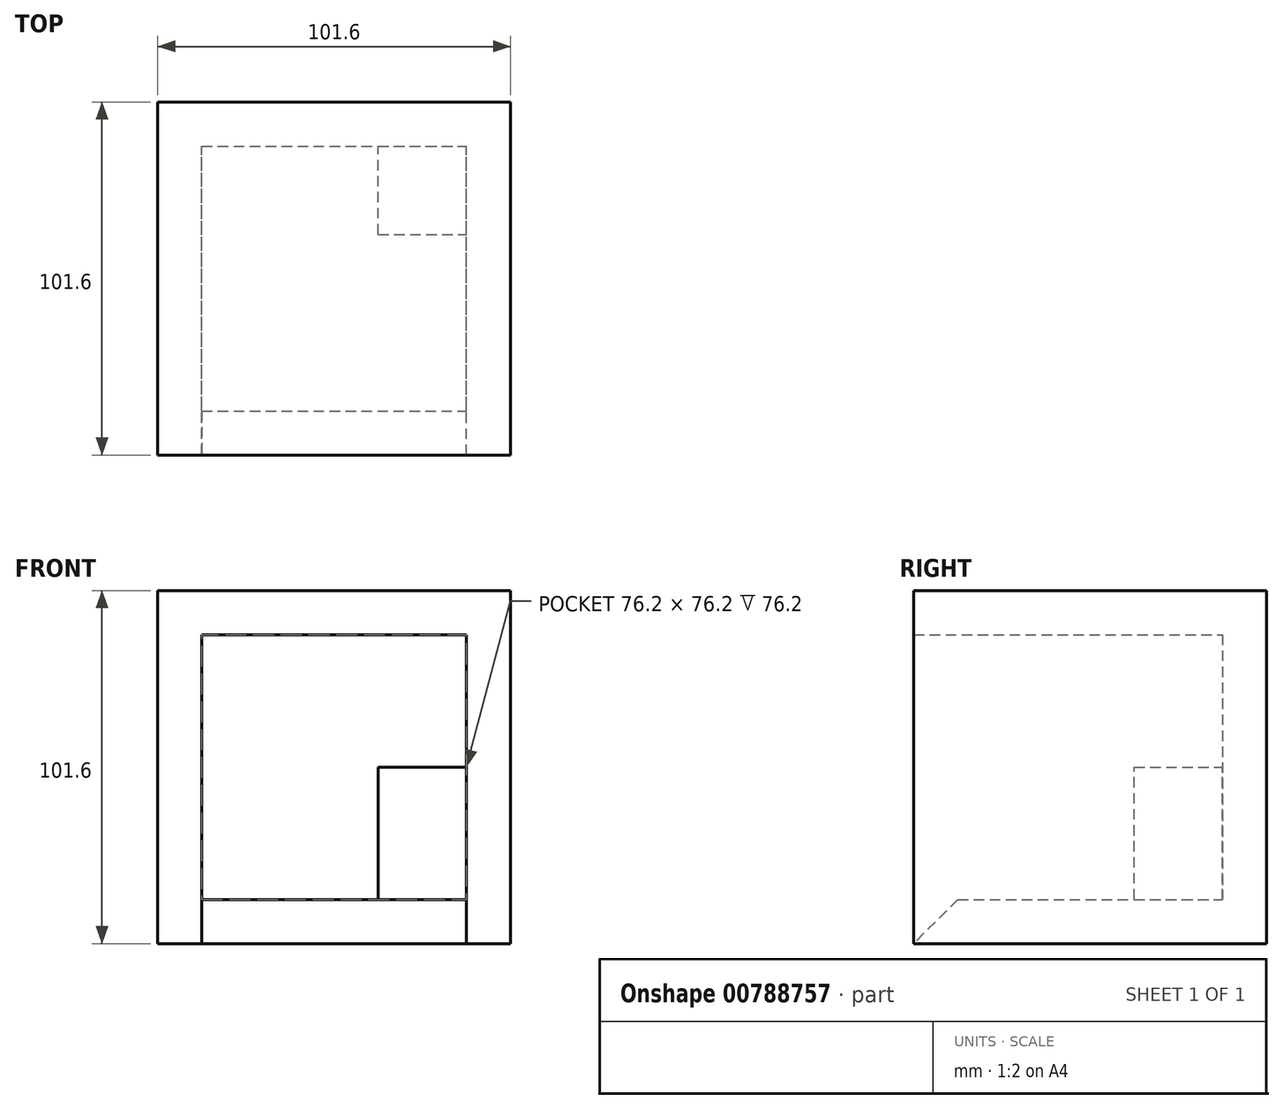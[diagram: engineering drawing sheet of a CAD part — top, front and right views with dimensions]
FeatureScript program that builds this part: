
annotation { "Feature Type Name" : "Feature", "Feature Type Description" : "" }
export const myFeature = defineFeature(function(context is Context, id is Id, definition is map)
    precondition{}
    {
        {
            var Q0;
            Q0=qCreatedBy(makeId("Front.planeOp"),FACE);
            var sketch = newSketch(context, id + "F0", { "sketchPlane" : qUnion([Q0])});
            skLineSegment(sketch, "E0.bottom", {"start": v(-44.9, 56.02) * mm, "end": v(56.7, 56.02) * mm});
            skLineSegment(sketch, "E0.top", {"start": v(-44.9, -45.58) * mm, "end": v(56.7, -45.58) * mm});
            skLineSegment(sketch, "E0.left", {"start": v(-44.9, 56.02) * mm, "end": v(-44.9, -45.58) * mm});
            skLineSegment(sketch, "E0.right", {"start": v(56.7, 56.02) * mm, "end": v(56.7, -45.58) * mm});
            skSolve(sketch);
        }
        {
            var Q0;
            Q0=makeQuery(id+"F0.imprint","IMPRINT",FACE,{"disambiguationData":[TD([[makeQuery(id+"F0.imprint","IMPRINT",EDGE,{"derivedFrom":sQuery(id+"F0.wireOp",EDGE,"E0.bottom")}),-1.0]])]});
            extrude(context, id + "F1", {"entities" : qUnion([Q0]), "depth" : 50.8 * mm, "offsetDistance" : 25.4 * mm, "hasSecondDirection" : true, "secondDirectionOppositeDirection" : true, "secondDirectionDepth" : 50.8 * mm});
        }
        {
            var Q0;
            Q0=makeQuery(id+"F1.opExtrude","CAP_FACE",FACE,{"disambiguationData":[OSD([sQuery(id+"F0.wireOp",EDGE,"E0.bottom"),sQuery(id+"F0.wireOp",EDGE,"E0.top"),sQuery(id+"F0.wireOp",EDGE,"E0.left"),sQuery(id+"F0.wireOp",EDGE,"E0.right")])],"isStart":false});
            shell(context, id + "F2", {"entities" : qUnion([Q0]), "thickness" : 12.7 * mm});
        }
        {
            var Q0;
            {var subQ0=sQuery(id+"F0.wireOp",EDGE,"E0.top");Q0=makeQuery(id+"F2.opShell","OFFSET_EDGE",EDGE,{"disambiguationData":[OSD([subQ0]),TDD([makeQuery(id+"F1.opExtrude","CAP_EDGE",EDGE,{"disambiguationData":[OSD([subQ0])],"isStart":false})])]});}
            chamfer(context, id + "F3", {"entities" : qUnion([Q0]), "width" : 12.7 * mm, "tangentPropagation" : true});
        }
        {
            var Q0;
            Q0=makeQuery(id+"F2.opShell","OFFSET_FACE",FACE,{"disambiguationData":[OSD([sQuery(id+"F0.wireOp",EDGE,"E0.bottom"),sQuery(id+"F0.wireOp",EDGE,"E0.top"),sQuery(id+"F0.wireOp",EDGE,"E0.left"),sQuery(id+"F0.wireOp",EDGE,"E0.right")])]});
            var sketch = newSketch(context, id + "F4", { "sketchPlane" : qUnion([Q0])});
            skLineSegment(sketch, "E1.bottom", {"start": v(18.6, -32.88) * mm, "end": v(44, -32.88) * mm});
            skLineSegment(sketch, "E1.top", {"start": v(18.6, 5.22) * mm, "end": v(44, 5.22) * mm});
            skLineSegment(sketch, "E1.left", {"start": v(18.6, -32.88) * mm, "end": v(18.6, 5.22) * mm});
            skLineSegment(sketch, "E1.right", {"start": v(44, -32.88) * mm, "end": v(44, 5.22) * mm});
            skSolve(sketch);
        }
        {
            var Q0;
            Q0=makeQuery(id+"F4.imprint","IMPRINT",FACE,{"disambiguationData":[TD([[makeQuery(id+"F4.imprint","IMPRINT",EDGE,{"derivedFrom":sQuery(id+"F4.wireOp",EDGE,"E1.bottom")}),1.0]])]});
            extrude(context, id + "F5", {"entities" : qUnion([Q0]), "depth" : 25.4 * mm, "offsetDistance" : 25.4 * mm});
        }
    });
